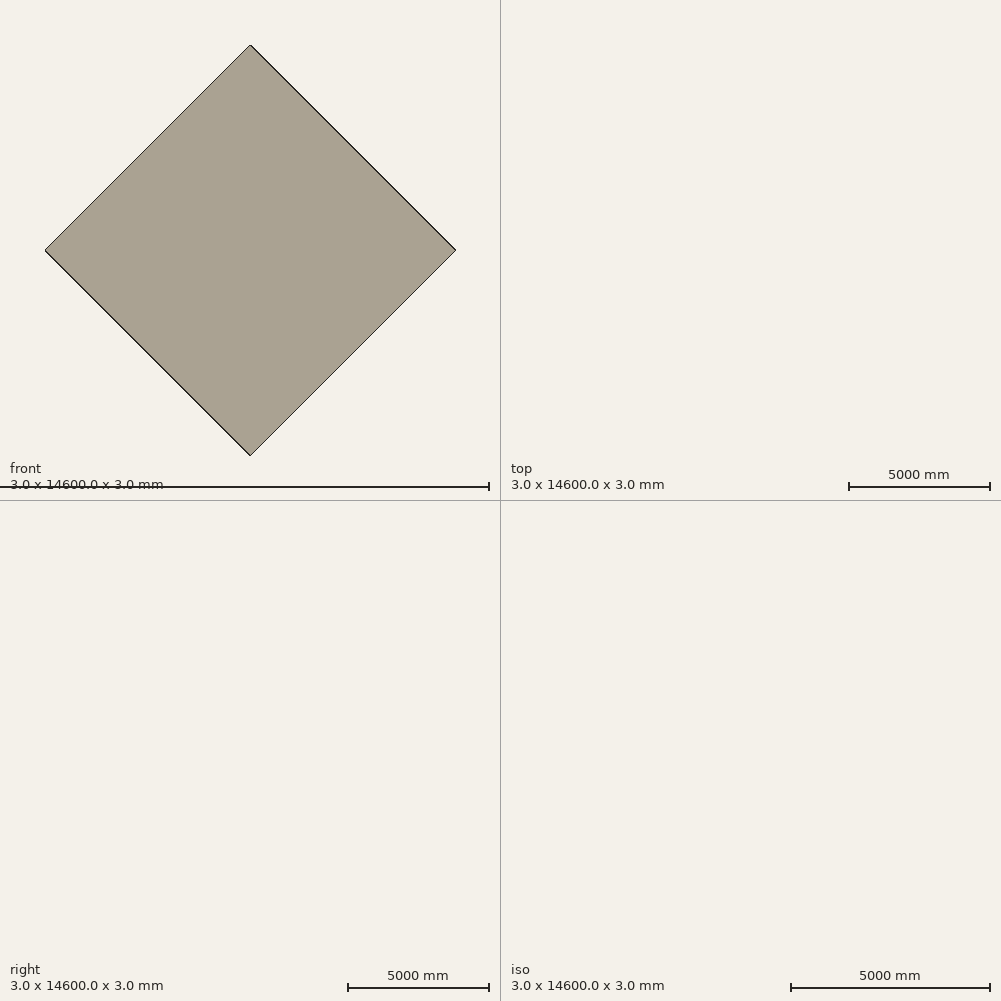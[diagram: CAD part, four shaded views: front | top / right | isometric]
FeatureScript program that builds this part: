
annotation { "Feature Type Name" : "Feature", "Feature Type Description" : "" }
export const myFeature = defineFeature(function(context is Context, id is Id, definition is map)
    precondition{}
    {
        {
            assignVariable(context, id + "F0", {"name" : "l", "anyValue" : 14600 * mm});
        }
        {
            var Q0;
            Q0=qCreatedBy(makeId("Front.planeOp"),FACE);
            var sketch = newSketch(context, id + "F1", { "sketchPlane" : qUnion([Q0])});
            skCircle(sketch, "E0", {"center": v(0, 0) * mm, "radius": 1.5 * mm});
            skSolve(sketch);
        }
        {
            var Q0;
            Q0=qSketchRegion(id+"F1",true);
            extrude(context, id + "F2", {"entities" : qUnion([Q0]), "depth" : getVariable(context, 'l'), "offsetDistance" : 25 * mm});
        }
    });
